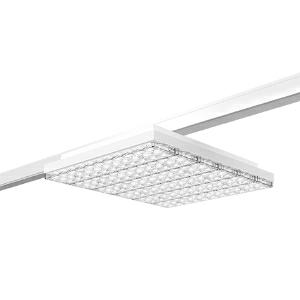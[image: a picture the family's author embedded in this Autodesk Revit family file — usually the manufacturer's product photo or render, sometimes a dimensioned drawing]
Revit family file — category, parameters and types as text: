
# Revit family: 3f_filippi_-_3f_six_blindo_ampio_3f_filippi_-_47698_-_3f_six_wh_85-840_wide_307x378
name_source: partatom
category: Lighting Fixtures
units: mm (PartAtom-declared; Revit-internal decimal feet)

## family parameters
Cut with Voids When Loaded = No
Host = Face
Light Source = No
Part Type = Normal
Room Calculation Point = No
Round Connector Dimension = Use Diameter
Shared = No

## types (1)
- 3F Filippi - 3F Six Blindo Ampio (1 x LED, 14086 lm, 83 W, 4000 K)
    Apparent Load = 83 VA
    Approval mark = CE
    CIE Flux Codes = 61 95 99 99 100
    Color Rendering = 80
    Color Temperature = 4000 K
    Control Gear = Electronic ballast
    Default Elevation = 1800 mm
    Description = ILLUMINOTECHNICAL
Luminous efficiency 100% (DLOR 99%, ULOR 1%).
Initial luminous flux of the luminaire 14086 lm.
Symmetric wide direct distribution.
Installation Interdistance Transv.D = 1.39 x hu - Long.D = 1.43 x hu.
Tabular UGR (CIE 117 - 4H-8H; S=0.25H; 70/50/20): RUG 23.9 - 24.2.
Beam angle: 102° - 103°.
Luminous efficacy 170 lm/W.
Lifetime (L93/B10): 30000 h. (tq+25°C)
Lifetime (L90/B10): 50000 h. (tq+25°C)
Lifetime (L85/B10): 80000 h. (tq+25°C)
Lifetime (L80/B10): 100000 h. (tq+25°C)
Lifetime (L85/B10): 50000 h. (tq+35°C)
Sudden decreased luminous flux after 50000 hours: 0% (C0).
Photobiological safety in compliance with IEC/TR 62778: RG0 risk exempt, (IEC 62471).
In compliance with IEC/EN 62722-2-1 - IEC/EN 62717 standards.

SOURCE
Linear LED module 85W/840.
Energy efficiency class (UE 2019/2020 - UE 2019/2015): C.
CIE 13.3 Colour rendering index: CRI >80 (R9 <50%).
IES TM-30 Fidelity Index: Rf = 84 Rg = 95.
CCT nominal colour temperature 4000 K.
Colour initial tolerance (MacAdam): SDCM 3.

MECHANICAL
Housing in galvannealed steel, painted in white epoxy-polyester.
Lenses for wide distribution, in transparent methacrylate (PMMA) with external flat surface.
Luminaire with limited surface temperature. - D - (EN 60598-2-24)
Dimensions: 307x378 mm, height 52 mm. Weight 3.305 kg.
IP40 protection degree.
Mechanical strength to impacts IK06 (1 joule).
Glow-wire test resistance 650°C.

ELECTRICAL
Halogen Free electronic wiring 230V-50/60Hz, power factor 0.97, THD <25%, constant output current, class I, 1 driver.
Power of the luminaire 83 W.
ENEC - CE.
SAFE FLICKER: PstLM=<1 and SVM=<0.4 (IEC TR 61547-1 and IEC TR 63158), to ensure a more comfortable and safe light.
Luminaire compliant with EN 60598-2-22 for power supply from a centralised emergency system CPSS (Central Power Supply System), not incorporated in the luminaire - high risk areas excluded. The default power and flux are 100% in AC and 100% in DC.
Ambient temperature from 0°C to +35°C.
Temperature class T6 max 85°C.
Power cable protrudes by 1 m with sheared end.
Relative humidity UR: <85%.

INSTALLATION
Ceiling / Suspended / Wall.

APPLICATIONS
Suitable product for food production plants (HACCP), IFS (Food Version 6), BRC (GSFS Food Version 7).
In commercial environments, exhibition areas, shops and stores.

WARNING
Luminaire designed for disposal/recycling at end-of-life.
Replaceable (LED only) light source by a professional. Replaceable control gear by a professional.
    Height = 52 mm  [stored 0.170604 ft]
    Lamp = 1 x LED
    Lamp Light Flux = 14086 lm
    Lamp Power = 83 W
    Lamp count = 1
    Length = 307 mm
    Lifetime = 50000 h
    Luminous efficacy = 170 lm/W
    Manufacturer = 3F Filippi
    ModVariant = No
    Model = 3F Filippi - 47698 - 3F Six WH 85-840 WIDE 307x378
    Mounting Place = Ceiling
    Mounting Type = Pendant
    Number of Poles = 1
    OnlyDefault = Yes
    Power Factor = 1
    Product Name = 3F Filippi - 3F Six Blindo Ampio
    Product group = pendant luminaire
    ProductGroupID = 9
    Protection Class = Protection class I
    Protection Degree = IP 40
    RLX_Detail_Level = 1
    RLX_Emergency_Light_Flux = 0 lm
    RLX_Emergency_Type = 0
    RLX_Emergency_Type_DB = No
    RlxData = <blob elided: 58373 chars, md5=9ecd88d9>
    Socket = socket
    Standby Power = 0 W
    System Light Flux = 14086 lm
    System Power = 83 W
    Type Comments = Product without accessories
    Type Image = 3ffilippi_3f_six_blindo.jpg
    URL = http://relux.com
    VarID = ---
    Voltage = 0 V
    Weight = 0.00 kg
    Width = 378 mm

note: [stored X ft] marks values corroborated as IEEE doubles in the binary element streams (Revit-internal decimal feet)

## geometry (parser evidence)
native form markers: Blend x4, Sweep x11
no freeform markers — native parametric forms only
